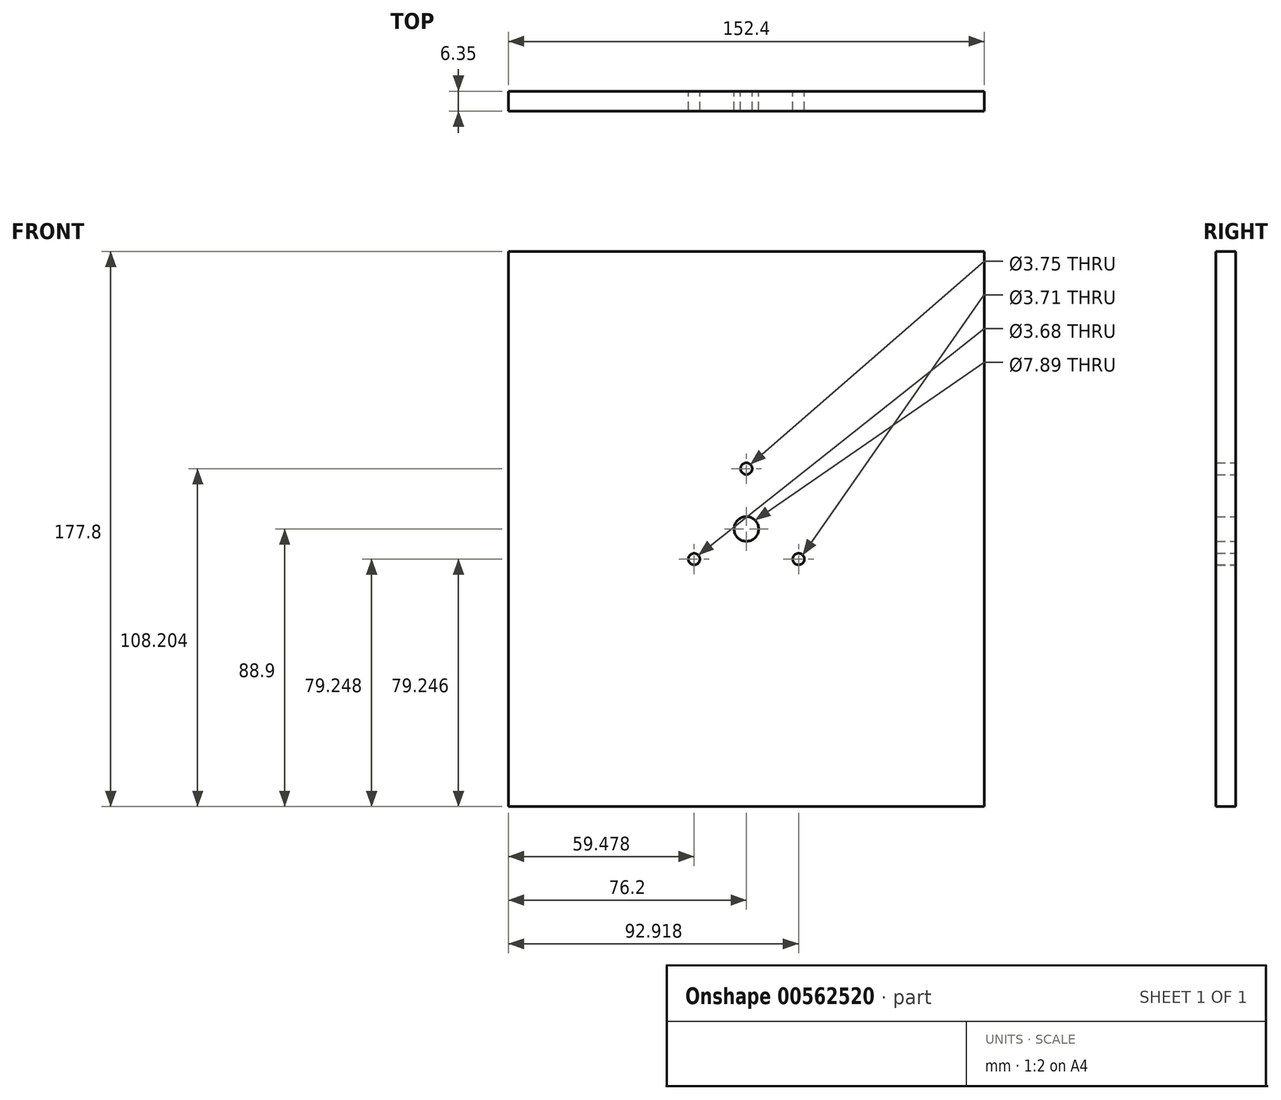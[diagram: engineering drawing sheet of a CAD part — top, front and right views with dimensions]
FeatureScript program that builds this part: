
annotation { "Feature Type Name" : "Feature", "Feature Type Description" : "" }
export const myFeature = defineFeature(function(context is Context, id is Id, definition is map)
    precondition{}
    {
        {
            var Q0;
            Q0=qCreatedBy(makeId("Front.planeOp"),FACE);
            var sketch = newSketch(context, id + "F0", { "sketchPlane" : qUnion([Q0])});
            skLineSegment(sketch, "E0.bottom", {"start": v(76.2, 88.9) * mm, "end": v(-76.2, 88.9) * mm});
            skLineSegment(sketch, "E0.top", {"start": v(76.2, -88.9) * mm, "end": v(-76.2, -88.9) * mm});
            skLineSegment(sketch, "E0.left", {"start": v(76.2, 88.9) * mm, "end": v(76.2, -88.9) * mm});
            skLineSegment(sketch, "E0.right", {"start": v(-76.2, 88.9) * mm, "end": v(-76.2, -88.9) * mm});
            skPoint(sketch, "E0.middle", {"position": v(0, 0) * mm});
            skLineSegment(sketch, "E1", {"start": v(0, 0) * mm, "end": v(0, 83.85) * mm, "construction": true});
            skLineSegment(sketch, "E2", {"start": v(0, 0) * mm, "end": v(67.53, -38.99) * mm, "construction": true});
            skLineSegment(sketch, "E3", {"start": v(0, 0) * mm, "end": v(-59.92, -34.6) * mm, "construction": true});
            skLineSegment(sketch, "E4", {"start": v(-11.78, 19.3) * mm, "end": v(15.02, 19.3) * mm, "construction": true});
            skLineSegment(sketch, "E5", {"start": v(20.55, -3.01) * mm, "end": v(11.36, -18.94) * mm, "construction": true});
            skLineSegment(sketch, "E6", {"start": v(-21.54, -0.84) * mm, "end": v(-10.74, -20.58) * mm, "construction": true});
            skCircle(sketch, "E7", {"center": v(-16.72, -9.65) * mm, "radius": 1.84 * mm});
            skCircle(sketch, "E8", {"center": v(16.72, -9.65) * mm, "radius": 1.85 * mm});
            skCircle(sketch, "E9", {"center": v(0, 19.3) * mm, "radius": 1.87 * mm});
            skCircle(sketch, "E10", {"center": v(0, 0) * mm, "radius": 3.94 * mm});
            skSolve(sketch);
        }
        {
            var Q0;
            Q0=makeQuery(id+"F0.imprint","IMPRINT",FACE,{"disambiguationData":[TD([[makeQuery(id+"F0.imprint","IMPRINT",EDGE,{"derivedFrom":sQuery(id+"F0.wireOp",EDGE,"E0.bottom")}),1.0]])]});
            extrude(context, id + "F1", {"entities" : qUnion([Q0]), "depth" : 6.35 * mm, "offsetDistance" : 25.4 * mm});
        }
    });
